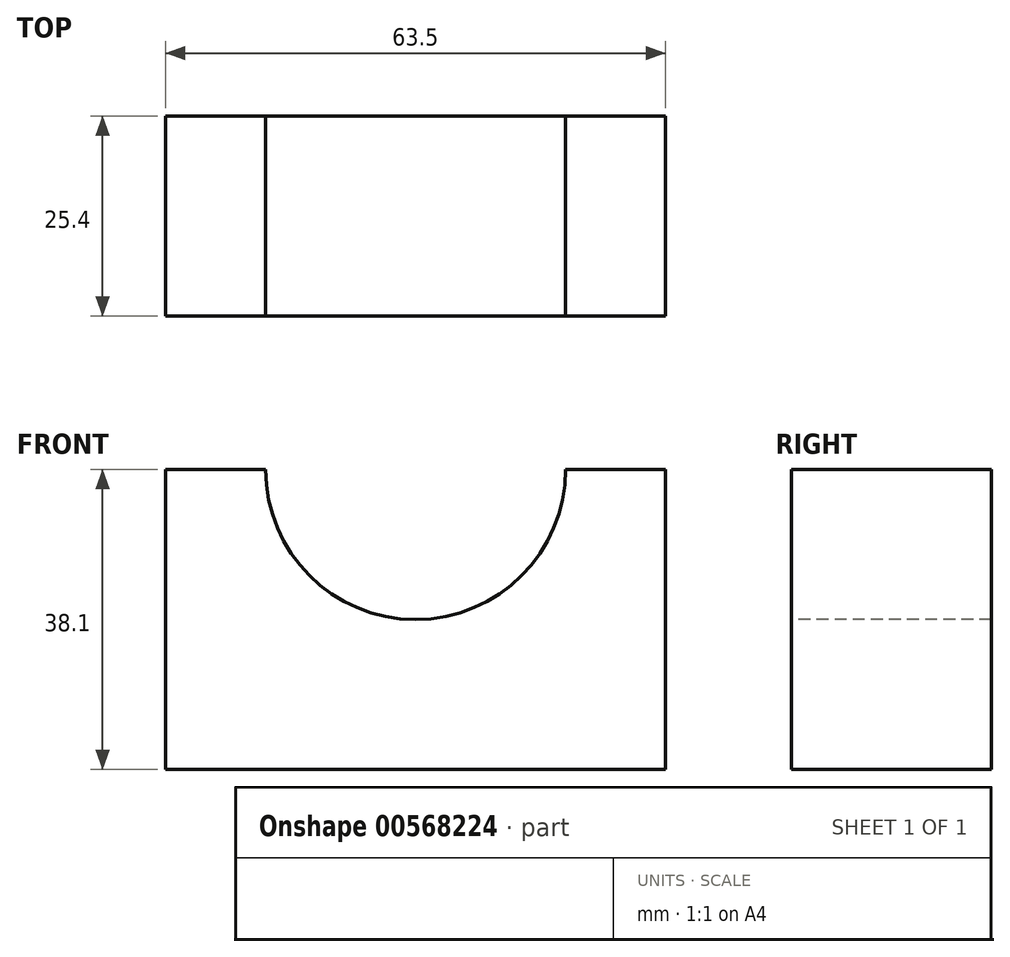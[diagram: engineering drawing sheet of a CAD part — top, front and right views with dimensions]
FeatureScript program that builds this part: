
annotation { "Feature Type Name" : "Feature", "Feature Type Description" : "" }
export const myFeature = defineFeature(function(context is Context, id is Id, definition is map)
    precondition{}
    {
        {
            var Q0;
            Q0=qCreatedBy(makeId("Front.planeOp"),FACE);
            var sketch = newSketch(context, id + "F0", { "sketchPlane" : qUnion([Q0])});
            skLineSegment(sketch, "E0", {"start": v(-29.44, 29.66) * mm, "end": v(34.06, 29.66) * mm});
            skLineSegment(sketch, "E1", {"start": v(34.06, 29.66) * mm, "end": v(34.06, -8.44) * mm});
            skLineSegment(sketch, "E2", {"start": v(34.06, -8.44) * mm, "end": v(-29.44, -8.44) * mm});
            skLineSegment(sketch, "E3", {"start": v(-29.44, -8.44) * mm, "end": v(-29.44, 29.66) * mm});
            skSolve(sketch);
        }
        {
            var Q0;
            Q0 = qSketchRegion(id + "F0", true);
            extrude(context, id + "F1", {"entities" : qUnion([Q0]), "depth" : 25.4 * mm, "offsetDistance" : 25.4 * mm});
        }
        {
            var Q0;
            Q0=makeQuery(id+"F1.opExtrude","CAP_FACE",FACE,{"disambiguationData":[OSD([sQuery(id+"F0.wireOp",EDGE,"E0"),sQuery(id+"F0.wireOp",EDGE,"E1"),sQuery(id+"F0.wireOp",EDGE,"E2"),sQuery(id+"F0.wireOp",EDGE,"E3")])],"isStart":false});
            var sketch = newSketch(context, id + "F2", { "sketchPlane" : qUnion([Q0])});
            skCircle(sketch, "E4", {"center": v(2.31, 29.66) * mm, "radius": 19.05 * mm});
            skSolve(sketch);
        }
        {
            var Q0;
            {var subQ0=sQuery(id+"F2.wireOp",EDGE,"E4");var subQ1=makeQuery(id+"F1.opExtrude","CAP_EDGE",EDGE,{"disambiguationData":[OSD([sQuery(id+"F0.wireOp",EDGE,"E0")])],"isStart":false});var subQ2=makeQuery(id+"F2.imprint","INTERSECT",VERTEX,{"disambiguationData":[OD(0.0)],"derivedFrom":[subQ1,subQ0]});Q0=makeQuery(id+"F2.imprint","IMPRINT",FACE,{"disambiguationData":[TD([[makeQuery(id+"F2.imprint","IMPRINT",EDGE,{"disambiguationData":[TD([[subQ2,-1.0]])],"derivedFrom":subQ0}),1.0]])]});}
            var Q1;
            {var subQ0=sQuery(id+"F2.wireOp",EDGE,"E4");var subQ1=makeQuery(id+"F1.opExtrude","CAP_EDGE",EDGE,{"disambiguationData":[OSD([sQuery(id+"F0.wireOp",EDGE,"E0")])],"isStart":false});var subQ2=makeQuery(id+"F2.imprint","INTERSECT",VERTEX,{"disambiguationData":[OD(0.0)],"derivedFrom":[subQ1,subQ0]});Q1=makeQuery(id+"F2.imprint","IMPRINT",FACE,{"disambiguationData":[TD([[makeQuery(id+"F2.imprint","IMPRINT",EDGE,{"disambiguationData":[TD([[subQ2,1.0]])],"derivedFrom":subQ0}),1.0]])]});}
            extrude(context, id + "F3", {"entities" : qUnion([Q0, Q1]), "operationType" : NewBodyOperationType.REMOVE, "oppositeDirection" : true, "depth" : 25.4 * mm, "offsetDistance" : 25.4 * mm});
        }
    });
